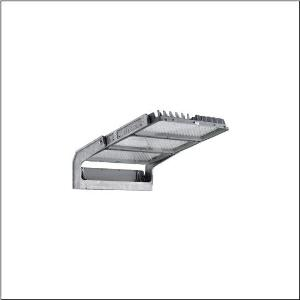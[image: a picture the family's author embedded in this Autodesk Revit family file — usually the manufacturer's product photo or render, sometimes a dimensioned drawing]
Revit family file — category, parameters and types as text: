
# Revit family: floodlight_fl_11_maxi_pro___rs12_5xa779124m01ab_02ca
name_source: partatom
category: Lighting Fixtures
units: mm (PartAtom-declared; Revit-internal decimal feet)

## family parameters
Cut with Voids When Loaded = No
Host = Face
Light Source = No
Part Type = Normal
Room Calculation Point = No
Round Connector Dimension = Use Diameter
Shared = No

## types (1)
- --- (1 x LED, 156610 lm, 1633.1 W, 5700K)
    Apparent Load = 1633 VA
    CIE Flux Codes = 79 92 99 100 100
    Color Rendering = 90
    Color Temperature = 5700K
    Default Elevation = 1800 mm
    Description = Floodlight FL 11  maxi  pro floodlight; light control with lens of PMMA; cover panel of toughened safety glass, transparent; light distribution: RS12, rotationally symmetric direct distribution, LED; colour temperature: 5700K, rated luminous flux: 156.610lm, colour rendering: CRI > 90, light colour: 957; luminous efficacy: 96lm/W; brightness control: DALI 2; with terminal, 5-pole, max. 2.5mm², mains connection: 220..240V/380..400V AC, 50/60Hz, surge voltage resistance: line to ground: 10kV, LED service life up to 100,000h L90. Typical operating time: 1000h per year., ECG replaceable separately, LED unit replaceable without ESD environment, dustproof LED module, dimming range 10..100%; 1633W floodlight with 3x LED unit of diecast aluminium, coated grey; length: 1.003mm / width: 651mm / height: 338mm; mounting bracket, of diecast aluminium, uncoated, natural, equipment: Power, protection rating (complete): IP66; insulation class (complete): insulation class I (protective earthing); certification: CE, ENEC, VDE; ball protection: ball impact resistant, only for outdoor installations in the designated locations, permissible operating ambient temperature: -40..+55°C, permissible storage temperature: -40..+85°Cpackaging unit: 1 piece

Light Distribution: RS12
    Height = 320 mm
    Lamp = 1 x LED
    Lamp Light Flux = 156610 lm
    Lamp Power = 1633.1 W
    Lamp count = 1
    Length = 1002 mm
    Luminous efficacy = 96 lm/W
    Manufacturer = Siteco
    ModVariant = No
    Model = 5XA779124M01AB
    Mounting Place = Ceiling
    Mounting Type = Surface mounted
    Number of Poles = 1
    OnlyDefault = Yes
    Power Factor = 1
    Product Name = Floodlight FL 11 maxi pro | RS12
    Product group = floodlight | ceiling mounted
    ProductGroupID = 303
    Protection Class = Protection class I
    Protection Degree = IP 66
    RLX_Detail_Level = 1
    RLX_Emergency_Light_Flux = 0 lm
    RLX_Emergency_Type = 0
    RLX_Emergency_Type_DB = No
    RlxData = <blob elided: 40241 chars, md5=bdba2b73>
    Socket = socket
    Standby Power = 0 W
    System Light Flux = 156610 lm
    System Power = 1633 W
    Type Comments = factory setting: luminous flux: 100 % | dim-lin: 254 | 1100 mA
    Type Image = l_1356210.jpg
    URL = http://relux.com
    VarID = @adj_039725
    Voltage = 0 V
    Weight = 0.00 kg
    Width = 655 mm

## geometry (parser evidence)
native form markers: Blend x4, Sweep x15
no freeform markers — native parametric forms only
